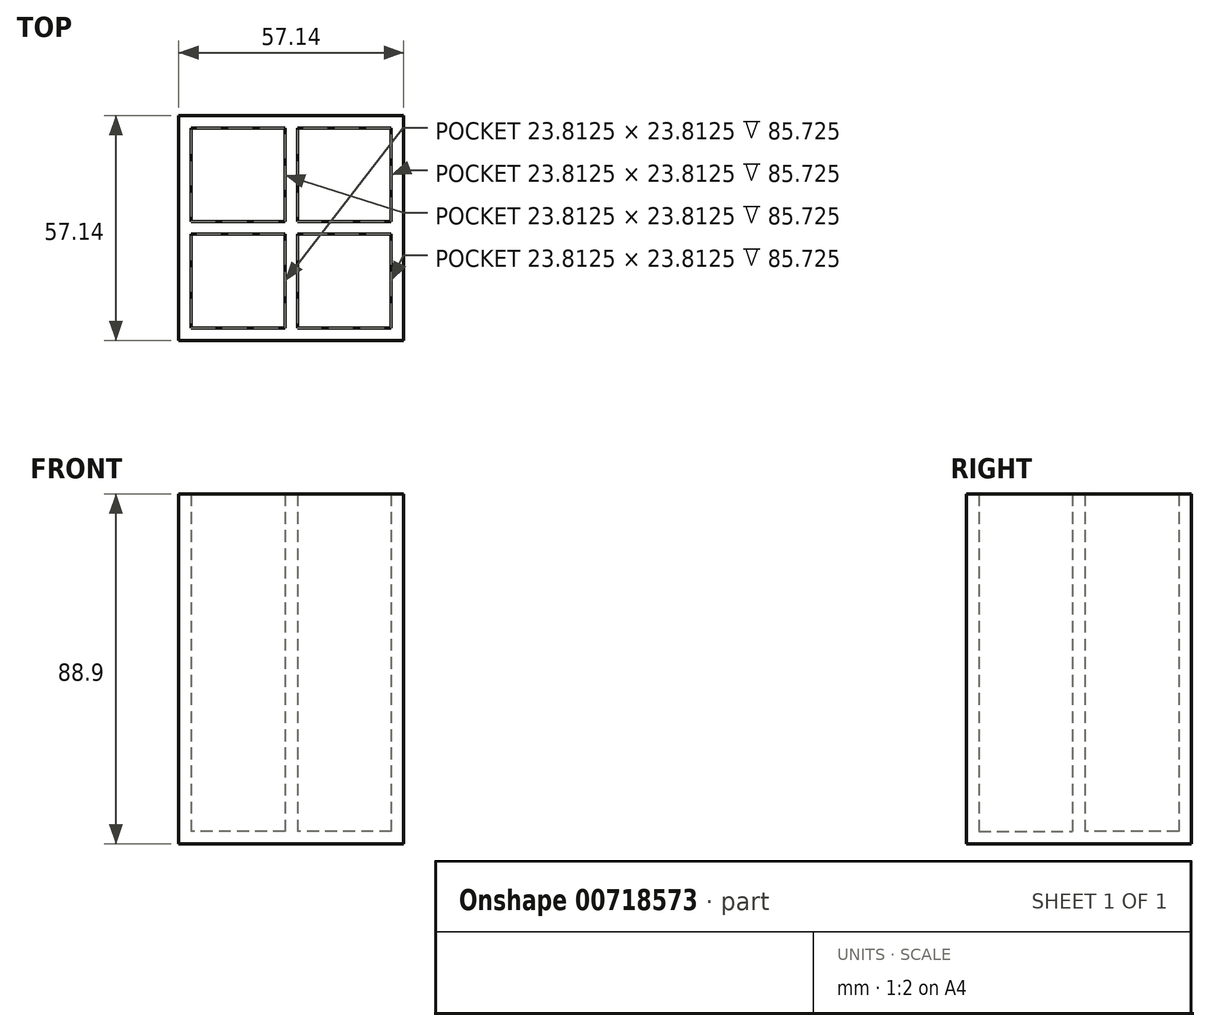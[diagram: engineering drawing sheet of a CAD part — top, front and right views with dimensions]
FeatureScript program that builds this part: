
annotation { "Feature Type Name" : "Feature", "Feature Type Description" : "" }
export const myFeature = defineFeature(function(context is Context, id is Id, definition is map)
    precondition{}
    {
        {
            var Q0;
            Q0=qCreatedBy(makeId("Top.planeOp"),FACE);
            var sketch = newSketch(context, id + "F0", { "sketchPlane" : qUnion([Q0])});
            skLineSegment(sketch, "E0.bottom", {"start": v(25.4, 25.4) * mm, "end": v(-25.4, 25.4) * mm});
            skLineSegment(sketch, "E0.top", {"start": v(25.4, -25.4) * mm, "end": v(-25.4, -25.4) * mm});
            skLineSegment(sketch, "E0.left", {"start": v(25.4, 25.4) * mm, "end": v(25.4, -25.4) * mm});
            skLineSegment(sketch, "E0.right", {"start": v(-25.4, 25.4) * mm, "end": v(-25.4, -25.4) * mm});
            skPoint(sketch, "E0.middle", {"position": v(0, 0) * mm});
            skSolve(sketch);
        }
        {
            var Q0;
            Q0 = qSketchRegion(id + "F0", true);
            extrude(context, id + "F1", {"entities" : qUnion([Q0]), "depth" : 3.17 * mm, "offsetDistance" : 25.4 * mm});
        }
        {
            var Q0;
            Q0=makeQuery(id+"F1.opExtrude","SWEPT_FACE",FACE,{"disambiguationData":[OSD([sQuery(id+"F0.wireOp",EDGE,"E0.left")])]});
            var sketch = newSketch(context, id + "F2", { "sketchPlane" : qUnion([Q0])});
            skLineSegment(sketch, "E1.bottom", {"start": v(-25.4, 0) * mm, "end": v(25.4, 0) * mm});
            skLineSegment(sketch, "E1.top", {"start": v(-25.4, 88.9) * mm, "end": v(25.4, 88.9) * mm});
            skLineSegment(sketch, "E1.left", {"start": v(-25.4, 0) * mm, "end": v(-25.4, 88.9) * mm});
            skLineSegment(sketch, "E1.right", {"start": v(25.4, 0) * mm, "end": v(25.4, 88.9) * mm});
            skSolve(sketch);
        }
        {
            var Q0;
            Q0 = qSketchRegion(id + "F2", true);
            extrude(context, id + "F3", {"entities" : qUnion([Q0]), "operationType" : NewBodyOperationType.ADD, "depth" : 3.17 * mm, "offsetDistance" : 25.4 * mm});
        }
        {
            var Q0;
            Q0=makeQuery(id+"F1.opExtrude","SWEPT_FACE",FACE,{"disambiguationData":[OSD([sQuery(id+"F0.wireOp",EDGE,"E0.right")])]});
            var sketch = newSketch(context, id + "F4", { "sketchPlane" : qUnion([Q0])});
            skLineSegment(sketch, "E2.bottom", {"start": v(-25.4, 0) * mm, "end": v(25.4, 0) * mm});
            skLineSegment(sketch, "E2.top", {"start": v(-25.4, 88.9) * mm, "end": v(25.4, 88.9) * mm});
            skLineSegment(sketch, "E2.left", {"start": v(-25.4, 0) * mm, "end": v(-25.4, 88.9) * mm});
            skLineSegment(sketch, "E2.right", {"start": v(25.4, 0) * mm, "end": v(25.4, 88.9) * mm});
            skSolve(sketch);
        }
        {
            var Q0;
            Q0 = qSketchRegion(id + "F4", true);
            extrude(context, id + "F5", {"entities" : qUnion([Q0]), "operationType" : NewBodyOperationType.ADD, "depth" : 3.17 * mm, "offsetDistance" : 25.4 * mm});
        }
        {
            var Q0;
            Q0=makeQuery(id+"F5.boolean.opBoolean","MERGE",FACE,{"derivedFrom":[makeQuery(id+"F3.boolean.opBoolean","MERGE",FACE,{"derivedFrom":[makeQuery(id+"F1.opExtrude","SWEPT_FACE",FACE,{"disambiguationData":[OSD([sQuery(id+"F0.wireOp",EDGE,"E0.top")])]}),makeQuery(id+"F3.opExtrude","SWEPT_FACE",FACE,{"disambiguationData":[OSD([sQuery(id+"F2.wireOp",EDGE,"E1.left")])]})]}),makeQuery(id+"F5.opExtrude","SWEPT_FACE",FACE,{"disambiguationData":[OSD([sQuery(id+"F4.wireOp",EDGE,"E2.right")])]})]});
            var sketch = newSketch(context, id + "F6", { "sketchPlane" : qUnion([Q0])});
            skLineSegment(sketch, "E3.bottom", {"start": v(-28.58, 0) * mm, "end": v(28.58, 0) * mm});
            skLineSegment(sketch, "E3.top", {"start": v(-28.58, 88.9) * mm, "end": v(28.58, 88.9) * mm});
            skLineSegment(sketch, "E3.left", {"start": v(-28.58, 0) * mm, "end": v(-28.58, 88.9) * mm});
            skLineSegment(sketch, "E3.right", {"start": v(28.58, 0) * mm, "end": v(28.58, 88.9) * mm});
            skSolve(sketch);
        }
        {
            var Q0;
            Q0 = qSketchRegion(id + "F6", true);
            extrude(context, id + "F7", {"entities" : qUnion([Q0]), "operationType" : NewBodyOperationType.ADD, "depth" : 3.17 * mm, "offsetDistance" : 25.4 * mm});
        }
        {
            var Q0;
            Q0=makeQuery(id+"F5.boolean.opBoolean","MERGE",FACE,{"derivedFrom":[makeQuery(id+"F3.boolean.opBoolean","MERGE",FACE,{"derivedFrom":[makeQuery(id+"F1.opExtrude","SWEPT_FACE",FACE,{"disambiguationData":[OSD([sQuery(id+"F0.wireOp",EDGE,"E0.bottom")])]}),makeQuery(id+"F3.opExtrude","SWEPT_FACE",FACE,{"disambiguationData":[OSD([sQuery(id+"F2.wireOp",EDGE,"E1.right")])]})]}),makeQuery(id+"F5.opExtrude","SWEPT_FACE",FACE,{"disambiguationData":[OSD([sQuery(id+"F4.wireOp",EDGE,"E2.left")])]})]});
            var sketch = newSketch(context, id + "F8", { "sketchPlane" : qUnion([Q0])});
            skLineSegment(sketch, "E4.bottom", {"start": v(-28.58, 0) * mm, "end": v(28.58, 0) * mm});
            skLineSegment(sketch, "E4.top", {"start": v(-28.58, 88.9) * mm, "end": v(28.58, 88.9) * mm});
            skLineSegment(sketch, "E4.left", {"start": v(-28.58, 0) * mm, "end": v(-28.58, 88.9) * mm});
            skLineSegment(sketch, "E4.right", {"start": v(28.58, 0) * mm, "end": v(28.58, 88.9) * mm});
            skSolve(sketch);
        }
        {
            var Q0;
            Q0 = qSketchRegion(id + "F8", true);
            extrude(context, id + "F9", {"entities" : qUnion([Q0]), "operationType" : NewBodyOperationType.ADD, "depth" : 3.17 * mm, "offsetDistance" : 25.4 * mm});
        }
        {
            var Q0;
            Q0=makeQuery(id+"F1.opExtrude","CAP_FACE",FACE,{"disambiguationData":[OSD([sQuery(id+"F0.wireOp",EDGE,"E0.bottom"),sQuery(id+"F0.wireOp",EDGE,"E0.top"),sQuery(id+"F0.wireOp",EDGE,"E0.left"),sQuery(id+"F0.wireOp",EDGE,"E0.right")])],"isStart":false});
            var sketch = newSketch(context, id + "F10", { "sketchPlane" : qUnion([Q0])});
            skLineSegment(sketch, "E5.bottom", {"start": v(-25.4, -1.59) * mm, "end": v(25.4, -1.59) * mm});
            skLineSegment(sketch, "E5.top", {"start": v(-25.4, 1.59) * mm, "end": v(25.4, 1.59) * mm});
            skLineSegment(sketch, "E5.left", {"start": v(-25.4, -1.59) * mm, "end": v(-25.4, 1.59) * mm});
            skLineSegment(sketch, "E5.right", {"start": v(25.4, -1.59) * mm, "end": v(25.4, 1.59) * mm});
            skSolve(sketch);
        }
        {
            var Q0;
            Q0 = qSketchRegion(id + "F10", true);
            extrude(context, id + "F11", {"entities" : qUnion([Q0]), "operationType" : NewBodyOperationType.ADD, "depth" : 85.72 * mm, "offsetDistance" : 25.4 * mm});
        }
        {
            var Q0;
            Q0=makeQuery(id+"F11.boolean.opBoolean","SPLIT",FACE,{"disambiguationData":[TD([makeQuery(id+"F11.opExtrude","SWEPT_FACE",FACE,{"disambiguationData":[OSD([sQuery(id+"F10.wireOp",EDGE,"E5.top")])]})])],"derivedFrom":makeQuery(id+"F1.opExtrude","CAP_FACE",FACE,{"disambiguationData":[OSD([sQuery(id+"F0.wireOp",EDGE,"E0.bottom"),sQuery(id+"F0.wireOp",EDGE,"E0.top"),sQuery(id+"F0.wireOp",EDGE,"E0.left"),sQuery(id+"F0.wireOp",EDGE,"E0.right")])],"isStart":false})});
            var sketch = newSketch(context, id + "F12", { "sketchPlane" : qUnion([Q0])});
            skLineSegment(sketch, "E6.bottom", {"start": v(-1.59, 25.4) * mm, "end": v(1.59, 25.4) * mm});
            skLineSegment(sketch, "E6.top", {"start": v(-1.59, 1.59) * mm, "end": v(1.59, 1.59) * mm});
            skLineSegment(sketch, "E6.left", {"start": v(-1.59, 25.4) * mm, "end": v(-1.59, 1.59) * mm});
            skLineSegment(sketch, "E6.right", {"start": v(1.59, 25.4) * mm, "end": v(1.59, 1.59) * mm});
            skSolve(sketch);
        }
        {
            var Q0;
            Q0 = qSketchRegion(id + "F12", true);
            extrude(context, id + "F13", {"entities" : qUnion([Q0]), "operationType" : NewBodyOperationType.ADD, "depth" : 85.72 * mm, "offsetDistance" : 25.4 * mm});
        }
        {
            var Q0;
            Q0=makeQuery(id+"F11.boolean.opBoolean","SPLIT",FACE,{"disambiguationData":[TD([makeQuery(id+"F11.opExtrude","SWEPT_FACE",FACE,{"disambiguationData":[OSD([sQuery(id+"F10.wireOp",EDGE,"E5.bottom")])]})])],"derivedFrom":makeQuery(id+"F1.opExtrude","CAP_FACE",FACE,{"disambiguationData":[OSD([sQuery(id+"F0.wireOp",EDGE,"E0.bottom"),sQuery(id+"F0.wireOp",EDGE,"E0.top"),sQuery(id+"F0.wireOp",EDGE,"E0.left"),sQuery(id+"F0.wireOp",EDGE,"E0.right")])],"isStart":false})});
            var sketch = newSketch(context, id + "F14", { "sketchPlane" : qUnion([Q0])});
            skLineSegment(sketch, "E7.bottom", {"start": v(-1.59, -25.4) * mm, "end": v(1.59, -25.4) * mm});
            skLineSegment(sketch, "E7.top", {"start": v(-1.59, -1.59) * mm, "end": v(1.59, -1.59) * mm});
            skLineSegment(sketch, "E7.left", {"start": v(-1.59, -25.4) * mm, "end": v(-1.59, -1.59) * mm});
            skLineSegment(sketch, "E7.right", {"start": v(1.59, -25.4) * mm, "end": v(1.59, -1.59) * mm});
            skSolve(sketch);
        }
        {
            var Q0;
            Q0 = qSketchRegion(id + "F14", true);
            extrude(context, id + "F15", {"entities" : qUnion([Q0]), "operationType" : NewBodyOperationType.ADD, "depth" : 85.72 * mm, "offsetDistance" : 25.4 * mm});
        }
    });
